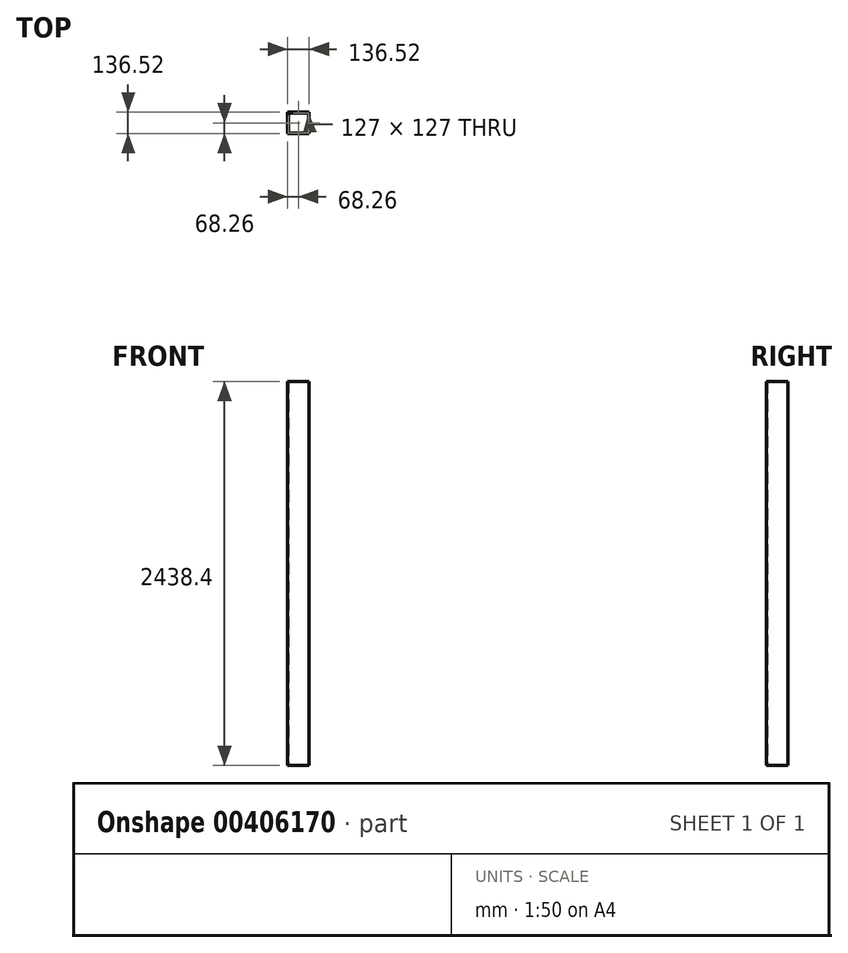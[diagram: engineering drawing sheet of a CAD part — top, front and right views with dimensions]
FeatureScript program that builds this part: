
annotation { "Feature Type Name" : "Feature", "Feature Type Description" : "" }
export const myFeature = defineFeature(function(context is Context, id is Id, definition is map)
    precondition{}
    {
        {
            var Q0;
            Q0=qCreatedBy(makeId("Top.planeOp"),FACE);
            var sketch = newSketch(context, id + "F0", { "sketchPlane" : qUnion([Q0])});
            skLineSegment(sketch, "E0.bottom", {"start": v(-31.45, 101.1) * mm, "end": v(95.55, 101.1) * mm});
            skLineSegment(sketch, "E0.top", {"start": v(-31.45, -25.9) * mm, "end": v(95.55, -25.9) * mm});
            skLineSegment(sketch, "E0.left", {"start": v(-31.45, 101.1) * mm, "end": v(-31.45, -25.9) * mm});
            skLineSegment(sketch, "E0.right", {"start": v(95.55, 101.1) * mm, "end": v(95.55, -25.9) * mm});
            skLineSegment(sketch, "E1.0", {"start": v(-36.21, -30.66) * mm, "end": v(100.31, -30.66) * mm});
            skLineSegment(sketch, "E1.1", {"start": v(-36.21, 105.86) * mm, "end": v(-36.21, -30.66) * mm});
            skLineSegment(sketch, "E1.2", {"start": v(-36.21, 105.86) * mm, "end": v(100.31, 105.86) * mm});
            skLineSegment(sketch, "E1.3", {"start": v(100.31, 105.86) * mm, "end": v(100.31, -30.66) * mm});
            skSolve(sketch);
        }
        {
            var Q0;
            Q0=makeQuery(id+"F0.imprint","IMPRINT",FACE,{"disambiguationData":[TD([[makeQuery(id+"F0.imprint","IMPRINT",EDGE,{"derivedFrom":sQuery(id+"F0.wireOp",EDGE,"E0.bottom")}),1.0]])]});
            var sketch = newSketch(context, id + "F1", { "sketchPlane" : qUnion([Q0])});
            skSolve(sketch);
        }
        {
            var Q0;
            Q0=makeQuery(id+"F1.imprint","IMPRINT",FACE,{"disambiguationData":[TD([[makeQuery(id+"F1.imprint","IMPRINT",EDGE,{"derivedFrom":makeQuery(id+"F0.imprint","IMPRINT",EDGE,{"derivedFrom":sQuery(id+"F0.wireOp",EDGE,"E0.bottom")})}),1.0]])]});
            extrude(context, id + "F2", {"entities" : qUnion([Q0]), "depth" : 2438.4 * mm});
        }
    });
